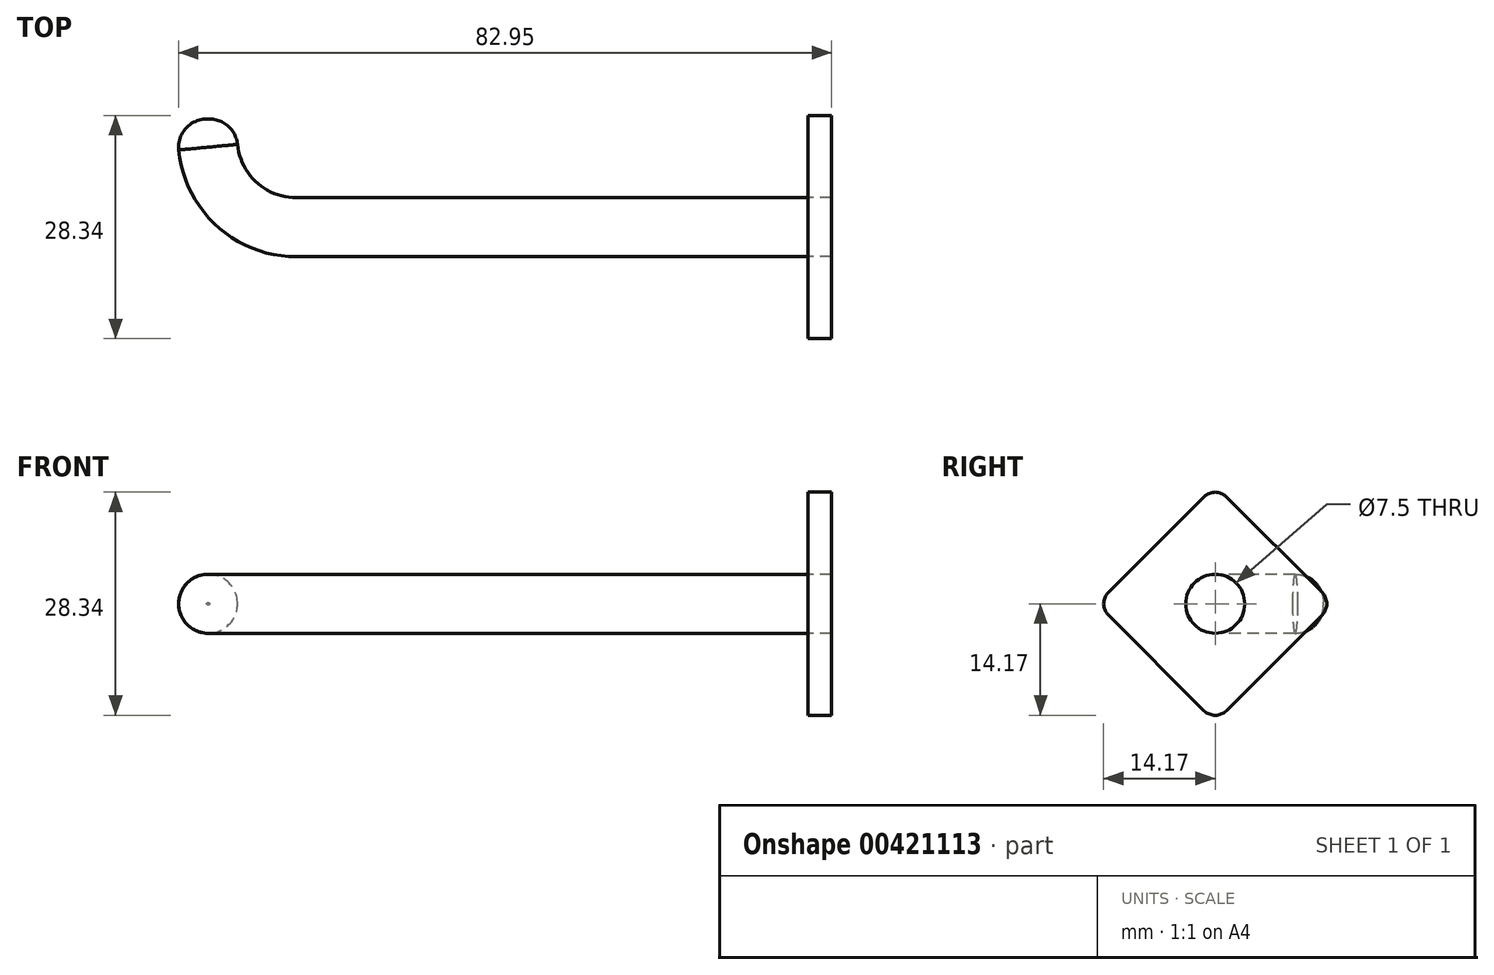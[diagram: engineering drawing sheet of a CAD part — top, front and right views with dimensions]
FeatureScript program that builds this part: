
annotation { "Feature Type Name" : "Feature", "Feature Type Description" : "" }
export const myFeature = defineFeature(function(context is Context, id is Id, definition is map)
    precondition{}
    {
        {
            var Q0;
            Q0=qCreatedBy(makeId("Top.planeOp"),FACE);
            var sketch = newSketch(context, id + "F0", { "sketchPlane" : qUnion([Q0])});
            skLineSegment(sketch, "E0.bottom", {"start": v(32.5, 3.75) * mm, "end": v(-32.5, 3.75) * mm});
            skLineSegment(sketch, "E0.top", {"start": v(32.5, -3.75) * mm, "end": v(-32.5, -3.75) * mm});
            skLineSegment(sketch, "E0.left", {"start": v(32.5, 3.75) * mm, "end": v(32.5, -3.75) * mm});
            skLineSegment(sketch, "E0.right", {"start": v(-32.5, 3.75) * mm, "end": v(-32.5, -3.75) * mm});
            skPoint(sketch, "E0.middle", {"position": v(0, 0) * mm});
            skCircle(sketch, "E1", {"center": v(-32.5, 11.25) * mm, "radius": 7.5 * mm});
            skCircle(sketch, "E2", {"center": v(-32.5, 11.25) * mm, "radius": 15 * mm});
            skLineSegment(sketch, "E3", {"start": v(-17.7, 13.75) * mm, "end": v(-47.3, 13.75) * mm});
            skSolve(sketch);
        }
        {
            var Q0;
            {var subQ4=sQuery(id+"F0.wireOp",EDGE,"E0.top");Q0=makeQuery(id+"F0.imprint","IMPRINT",FACE,{"disambiguationData":[TD([[makeQuery(id+"F0.imprint","IMPRINT",EDGE,{"derivedFrom":subQ4}),-1.0]])]});}
            var Q1;
            {var subQ0=sQuery(id+"F0.wireOp",EDGE,"E0.right");Q1=makeQuery(id+"F0.imprint","IMPRINT",FACE,{"disambiguationData":[TD([[makeQuery(id+"F0.imprint","IMPRINT",EDGE,{"derivedFrom":subQ0}),1.0]])]});}
            var Q2;
            {var subQ0=sQuery(id+"F0.wireOp",EDGE,"E0.right");Q2=makeQuery(id+"F0.imprint","IMPRINT",FACE,{"disambiguationData":[TD([[makeQuery(id+"F0.imprint","IMPRINT",EDGE,{"derivedFrom":subQ0}),-1.0]])]});}
            extrude(context, id + "F1", {"entities" : qUnion([Q0, Q1, Q2]), "depth" : 7.5 * mm, "symmetric" : true});
        }
        {
            var Q0;
            Q0=makeQuery(id+"F1.opExtrude","CAP_EDGE",EDGE,{"disambiguationData":[OSD([sQuery(id+"F0.wireOp",EDGE,"E0.bottom")])],"isStart":false});
            var Q1;
            Q1=makeQuery(id+"F1.opExtrude","CAP_EDGE",EDGE,{"disambiguationData":[OSD([sQuery(id+"F0.wireOp",EDGE,"E0.bottom")])],"isStart":true});
            var Q2;
            Q2=makeQuery(id+"F1.opExtrude","CAP_EDGE",EDGE,{"disambiguationData":[OSD([sQuery(id+"F0.wireOp",EDGE,"E0.top")])],"isStart":false});
            var Q3;
            Q3=makeQuery(id+"F1.opExtrude","CAP_EDGE",EDGE,{"disambiguationData":[OSD([sQuery(id+"F0.wireOp",EDGE,"E0.top")])],"isStart":true});
            fillet(context, id + "F2", {"entities" : qUnion([Q0, Q1, Q2, Q3]), "radius" : 3.75 * mm, "tangentPropagation" : true, "allowEdgeOverflow" : false});
        }
        {
            var Q0;
            Q0=makeQuery(id+"F1.opExtrude","SWEPT_FACE",FACE,{"disambiguationData":[OSD([sQuery(id+"F0.wireOp",EDGE,"E3")])]});
            fillet(context, id + "F3", {"entities" : qUnion([Q0]), "radius" : 3.59 * mm, "tangentPropagation" : true, "allowEdgeOverflow" : false});
        }
        {
            var Q0;
            Q0=makeQuery(id+"F1.opExtrude","SWEPT_FACE",FACE,{"disambiguationData":[OSD([sQuery(id+"F0.wireOp",EDGE,"E0.left")])]});
            var sketch = newSketch(context, id + "F4", { "sketchPlane" : qUnion([Q0])});
            skPoint(sketch, "E4.middle", {"position": v(0, 0) * mm});
            skCircle(sketch, "E5.cCircle", {"center": v(0, 0) * mm, "radius": 15 * mm, "construction": true});
            skLineSegment(sketch, "E5.0", {"start": v(15, 0) * mm, "end": v(0, -15) * mm});
            skLineSegment(sketch, "E5.1", {"start": v(0, -15) * mm, "end": v(-15, 0) * mm});
            skLineSegment(sketch, "E5.2", {"start": v(-15, 0) * mm, "end": v(0, 15) * mm});
            skLineSegment(sketch, "E5.3", {"start": v(0, 15) * mm, "end": v(15, 0) * mm});
            skSolve(sketch);
        }
        {
            var Q0;
            Q0=makeQuery(id+"F4.imprint","IMPRINT",FACE,{"disambiguationData":[TD([[makeQuery(id+"F4.imprint","IMPRINT",EDGE,{"derivedFrom":sQuery(id+"F4.wireOp",EDGE,"E5.0")}),-1.0]])]});
            var Q1;
            Q1=makeQuery(id+"F4.imprint","IMPRINT",FACE,{"disambiguationData":[TD([[makeQuery(id+"F4.imprint","IMPRINT",EDGE,{"derivedFrom":makeQuery(id+"F2.opFillet","BLEND_EDGE",EDGE,{"blendedFrom":[makeQuery(id+"F1.opExtrude","CAP_EDGE",EDGE,{"disambiguationData":[OSD([sQuery(id+"F0.wireOp",EDGE,"E0.top")])],"isStart":false}),makeQuery(id+"F1.opExtrude","SWEPT_FACE",FACE,{"disambiguationData":[OSD([sQuery(id+"F0.wireOp",EDGE,"E0.left")])]})],"blendedInto":[makeQuery(id+"F1.opExtrude","SWEPT_FACE",FACE,{"disambiguationData":[OSD([sQuery(id+"F0.wireOp",EDGE,"E0.left")])]})]})}),1.0]])]});
            extrude(context, id + "F5", {"entities" : qUnion([Q0, Q1]), "operationType" : NewBodyOperationType.ADD, "depth" : 3 * mm});
        }
        {
            var Q0;
            Q0=makeQuery(id+"F5.opExtrude","SWEPT_EDGE",EDGE,{"disambiguationData":[OSD([sQuery(id+"F4.wireOp",EDGE,"E5.1"),sQuery(id+"F4.wireOp",EDGE,"E5.2")])]});
            var Q1;
            Q1=makeQuery(id+"F5.opExtrude","SWEPT_EDGE",EDGE,{"disambiguationData":[OSD([sQuery(id+"F4.wireOp",EDGE,"E5.2"),sQuery(id+"F4.wireOp",EDGE,"E5.3")])]});
            var Q2;
            Q2=makeQuery(id+"F5.opExtrude","SWEPT_EDGE",EDGE,{"disambiguationData":[OSD([sQuery(id+"F4.wireOp",EDGE,"E5.0"),sQuery(id+"F4.wireOp",EDGE,"E5.3")])]});
            var Q3;
            Q3=makeQuery(id+"F5.opExtrude","SWEPT_EDGE",EDGE,{"disambiguationData":[OSD([sQuery(id+"F4.wireOp",EDGE,"E5.0"),sQuery(id+"F4.wireOp",EDGE,"E5.1")])]});
            fillet(context, id + "F6", {"entities" : qUnion([Q0, Q1, Q2, Q3]), "radius" : 2 * mm, "tangentPropagation" : true, "allowEdgeOverflow" : false});
        }
    });
